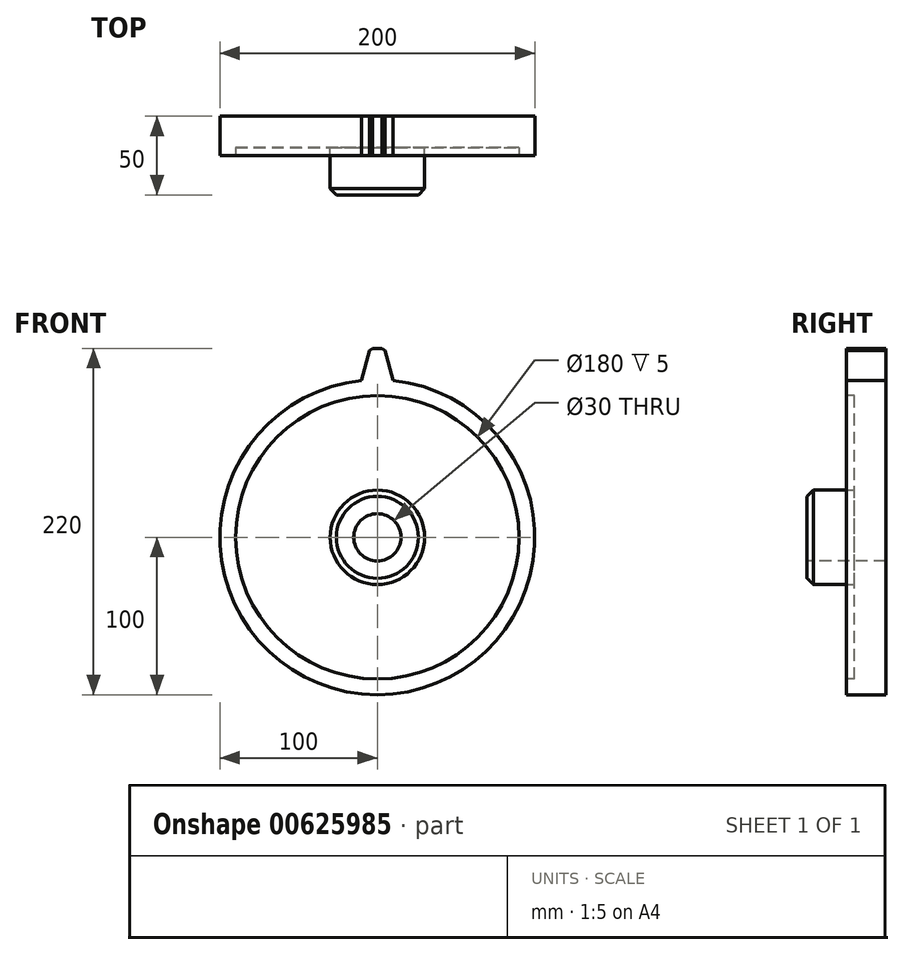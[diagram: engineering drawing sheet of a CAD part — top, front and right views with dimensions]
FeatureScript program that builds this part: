
annotation { "Feature Type Name" : "Feature", "Feature Type Description" : "" }
export const myFeature = defineFeature(function(context is Context, id is Id, definition is map)
    precondition{}
    {
        {
            var Q0;
            Q0=qCreatedBy(makeId("Front.planeOp"),FACE);
            var sketch = newSketch(context, id + "F0", { "sketchPlane" : qUnion([Q0])});
            skCircle(sketch, "E0", {"center": v(0, 0) * mm, "radius": 100 * mm});
            skSolve(sketch);
        }
        {
            var Q0;
            Q0 = qSketchRegion(id + "F0", true);
            extrude(context, id + "F1", {"entities" : qUnion([Q0]), "depth" : 25 * mm, "offsetDistance" : 25 * mm});
        }
        {
            var Q0;
            Q0=makeQuery(id+"F1.opExtrude","CAP_FACE",FACE,{"disambiguationData":[OSD([sQuery(id+"F0.wireOp",EDGE,"E0")])],"isStart":false});
            var sketch = newSketch(context, id + "F2", { "sketchPlane" : qUnion([Q0])});
            skLineSegment(sketch, "E1", {"start": v(-10, 99.5) * mm, "end": v(-4.5, 120) * mm});
            skLineSegment(sketch, "E2", {"start": v(-4.5, 120) * mm, "end": v(4.5, 120) * mm});
            skLineSegment(sketch, "E3", {"start": v(4.5, 120) * mm, "end": v(10, 99.5) * mm});
            skLineSegment(sketch, "E4", {"start": v(10, 99.5) * mm, "end": v(-10, 99.5) * mm});
            skSolve(sketch);
        }
        {
            var Q0;
            Q0 = qSketchRegion(id + "F2", true);
            extrude(context, id + "F3", {"entities" : qUnion([Q0]), "operationType" : NewBodyOperationType.ADD, "oppositeDirection" : true, "depth" : 25 * mm, "offsetDistance" : 25 * mm});
        }
        {
            var Q0;
            Q0=makeQuery(id+"F3.opExtrude","SWEPT_EDGE",EDGE,{"disambiguationData":[OSD([sQuery(id+"F0.wireOp",EDGE,"E0"),sQuery(id+"F2.wireOp",EDGE,"E3"),sQuery(id+"F2.wireOp",EDGE,"E4")])]});
            var Q1;
            Q1=makeQuery(id+"F3.opExtrude","SWEPT_EDGE",EDGE,{"disambiguationData":[OSD([sQuery(id+"F0.wireOp",EDGE,"E0"),sQuery(id+"F2.wireOp",EDGE,"E1"),sQuery(id+"F2.wireOp",EDGE,"E4")])]});
            fillet(context, id + "F4", {"entities" : qUnion([Q0, Q1]), "radius" : 5 * mm, "tangentPropagation" : true, "allowEdgeOverflow" : false});
        }
        {
            var Q0;
            Q0=makeQuery(id+"F3.opExtrude","SWEPT_EDGE",EDGE,{"disambiguationData":[OSD([sQuery(id+"F2.wireOp",EDGE,"E1"),sQuery(id+"F2.wireOp",EDGE,"E2")])]});
            var Q1;
            Q1=makeQuery(id+"F3.opExtrude","SWEPT_EDGE",EDGE,{"disambiguationData":[OSD([sQuery(id+"F2.wireOp",EDGE,"E2"),sQuery(id+"F2.wireOp",EDGE,"E3")])]});
            chamfer(context, id + "F5", {"entities" : qUnion([Q0, Q1]), "width" : 2 * mm, "tangentPropagation" : true});
        }
        {
            var Q0;
            {var subQ0=sQuery(id+"F2.wireOp",EDGE,"E4");var subQ1=sQuery(id+"F2.wireOp",EDGE,"E3");var subQ2=sQuery(id+"F2.wireOp",EDGE,"E2");var subQ3=sQuery(id+"F2.wireOp",EDGE,"E1");Q0=makeQuery(id+"FDIh3SWYxGmvvfI_1.19.F3.boolean.opBoolean","MERGE",FACE,{"derivedFrom":[makeQuery(id+"FDIh3SWYxGmvvfI_1.18.F3.boolean.opBoolean","MERGE",FACE,{"derivedFrom":[makeQuery(id+"FDIh3SWYxGmvvfI_1.17.F3.boolean.opBoolean","MERGE",FACE,{"derivedFrom":[makeQuery(id+"FDIh3SWYxGmvvfI_1.16.F3.boolean.opBoolean","MERGE",FACE,{"derivedFrom":[makeQuery(id+"FDIh3SWYxGmvvfI_1.15.F3.boolean.opBoolean","MERGE",FACE,{"derivedFrom":[makeQuery(id+"FDIh3SWYxGmvvfI_1.14.F3.boolean.opBoolean","MERGE",FACE,{"derivedFrom":[makeQuery(id+"FDIh3SWYxGmvvfI_1.13.F3.boolean.opBoolean","MERGE",FACE,{"derivedFrom":[makeQuery(id+"FDIh3SWYxGmvvfI_1.12.F3.boolean.opBoolean","MERGE",FACE,{"derivedFrom":[makeQuery(id+"FDIh3SWYxGmvvfI_1.11.F3.boolean.opBoolean","MERGE",FACE,{"derivedFrom":[makeQuery(id+"FDIh3SWYxGmvvfI_1.10.F3.boolean.opBoolean","MERGE",FACE,{"derivedFrom":[makeQuery(id+"FDIh3SWYxGmvvfI_1.9.F3.boolean.opBoolean","MERGE",FACE,{"derivedFrom":[makeQuery(id+"FDIh3SWYxGmvvfI_1.8.F3.boolean.opBoolean","MERGE",FACE,{"derivedFrom":[makeQuery(id+"FDIh3SWYxGmvvfI_1.7.F3.boolean.opBoolean","MERGE",FACE,{"derivedFrom":[makeQuery(id+"FDIh3SWYxGmvvfI_1.6.F3.boolean.opBoolean","MERGE",FACE,{"derivedFrom":[makeQuery(id+"FDIh3SWYxGmvvfI_1.5.F3.boolean.opBoolean","MERGE",FACE,{"derivedFrom":[makeQuery(id+"FDIh3SWYxGmvvfI_1.4.F3.boolean.opBoolean","MERGE",FACE,{"derivedFrom":[makeQuery(id+"FDIh3SWYxGmvvfI_1.3.F3.boolean.opBoolean","MERGE",FACE,{"derivedFrom":[makeQuery(id+"FDIh3SWYxGmvvfI_1.2.F3.boolean.opBoolean","MERGE",FACE,{"derivedFrom":[makeQuery(id+"FDIh3SWYxGmvvfI_1.1.F3.boolean.opBoolean","MERGE",FACE,{"derivedFrom":[makeQuery(id+"F3.boolean.opBoolean","MERGE",FACE,{"derivedFrom":[makeQuery(id+"F1.opExtrude","CAP_FACE",FACE,{"disambiguationData":[OSD([sQuery(id+"F0.wireOp",EDGE,"E0")])],"isStart":false}),makeQuery(id+"F3.opExtrude","CAP_FACE",FACE,{"disambiguationData":[OSD([subQ3,subQ2,subQ1,subQ0])],"isStart":true})]}),makeQuery(id+"FDIh3SWYxGmvvfI_1.1.F3.opExtrude","CAP_FACE",FACE,{"disambiguationData":[OSD([subQ3,subQ2,subQ1,subQ0])],"isStart":true})]}),makeQuery(id+"FDIh3SWYxGmvvfI_1.2.F3.opExtrude","CAP_FACE",FACE,{"disambiguationData":[OSD([subQ3,subQ2,subQ1,subQ0])],"isStart":true})]}),makeQuery(id+"FDIh3SWYxGmvvfI_1.3.F3.opExtrude","CAP_FACE",FACE,{"disambiguationData":[OSD([subQ3,subQ2,subQ1,subQ0])],"isStart":true})]}),makeQuery(id+"FDIh3SWYxGmvvfI_1.4.F3.opExtrude","CAP_FACE",FACE,{"disambiguationData":[OSD([subQ3,subQ2,subQ1,subQ0])],"isStart":true})]}),makeQuery(id+"FDIh3SWYxGmvvfI_1.5.F3.opExtrude","CAP_FACE",FACE,{"disambiguationData":[OSD([subQ3,subQ2,subQ1,subQ0])],"isStart":true})]}),makeQuery(id+"FDIh3SWYxGmvvfI_1.6.F3.opExtrude","CAP_FACE",FACE,{"disambiguationData":[OSD([subQ3,subQ2,subQ1,subQ0])],"isStart":true})]}),makeQuery(id+"FDIh3SWYxGmvvfI_1.7.F3.opExtrude","CAP_FACE",FACE,{"disambiguationData":[OSD([subQ3,subQ2,subQ1,subQ0])],"isStart":true})]}),makeQuery(id+"FDIh3SWYxGmvvfI_1.8.F3.opExtrude","CAP_FACE",FACE,{"disambiguationData":[OSD([subQ3,subQ2,subQ1,subQ0])],"isStart":true})]}),makeQuery(id+"FDIh3SWYxGmvvfI_1.9.F3.opExtrude","CAP_FACE",FACE,{"disambiguationData":[OSD([subQ3,subQ2,subQ1,subQ0])],"isStart":true})]}),makeQuery(id+"FDIh3SWYxGmvvfI_1.10.F3.opExtrude","CAP_FACE",FACE,{"disambiguationData":[OSD([subQ3,subQ2,subQ1,subQ0])],"isStart":true})]}),makeQuery(id+"FDIh3SWYxGmvvfI_1.11.F3.opExtrude","CAP_FACE",FACE,{"disambiguationData":[OSD([subQ3,subQ2,subQ1,subQ0])],"isStart":true})]}),makeQuery(id+"FDIh3SWYxGmvvfI_1.12.F3.opExtrude","CAP_FACE",FACE,{"disambiguationData":[OSD([subQ3,subQ2,subQ1,subQ0])],"isStart":true})]}),makeQuery(id+"FDIh3SWYxGmvvfI_1.13.F3.opExtrude","CAP_FACE",FACE,{"disambiguationData":[OSD([subQ3,subQ2,subQ1,subQ0])],"isStart":true})]}),makeQuery(id+"FDIh3SWYxGmvvfI_1.14.F3.opExtrude","CAP_FACE",FACE,{"disambiguationData":[OSD([subQ3,subQ2,subQ1,subQ0])],"isStart":true})]}),makeQuery(id+"FDIh3SWYxGmvvfI_1.15.F3.opExtrude","CAP_FACE",FACE,{"disambiguationData":[OSD([subQ3,subQ2,subQ1,subQ0])],"isStart":true})]}),makeQuery(id+"FDIh3SWYxGmvvfI_1.16.F3.opExtrude","CAP_FACE",FACE,{"disambiguationData":[OSD([subQ3,subQ2,subQ1,subQ0])],"isStart":true})]}),makeQuery(id+"FDIh3SWYxGmvvfI_1.17.F3.opExtrude","CAP_FACE",FACE,{"disambiguationData":[OSD([subQ3,subQ2,subQ1,subQ0])],"isStart":true})]}),makeQuery(id+"FDIh3SWYxGmvvfI_1.18.F3.opExtrude","CAP_FACE",FACE,{"disambiguationData":[OSD([subQ3,subQ2,subQ1,subQ0])],"isStart":true})]}),makeQuery(id+"FDIh3SWYxGmvvfI_1.19.F3.opExtrude","CAP_FACE",FACE,{"disambiguationData":[OSD([subQ3,subQ2,subQ1,subQ0])],"isStart":true})]});}
            var sketch = newSketch(context, id + "F6", { "sketchPlane" : qUnion([Q0])});
            skCircle(sketch, "E5", {"center": v(0, 0) * mm, "radius": 90 * mm});
            skSolve(sketch);
        }
        {
            var Q0;
            Q0=makeQuery(id+"F6.imprint","IMPRINT",FACE,{"disambiguationData":[TD([[makeQuery(id+"F6.imprint","IMPRINT",EDGE,{"derivedFrom":sQuery(id+"F6.wireOp",EDGE,"E5")}),1.0]])]});
            extrude(context, id + "F7", {"entities" : qUnion([Q0]), "operationType" : NewBodyOperationType.REMOVE, "oppositeDirection" : true, "depth" : 5 * mm, "offsetDistance" : 25 * mm});
        }
        {
            var Q0;
            Q0=makeQuery(id+"F7.boolean.opBoolean","COPY",FACE,{"derivedFrom":makeQuery(id+"F7.opExtrude","CAP_FACE",FACE,{"disambiguationData":[OSD([sQuery(id+"F6.wireOp",EDGE,"E5")])],"isStart":false})});
            var sketch = newSketch(context, id + "F8", { "sketchPlane" : qUnion([Q0])});
            skCircle(sketch, "E6", {"center": v(0, 0) * mm, "radius": 30 * mm});
            skSolve(sketch);
        }
        {
            var Q0;
            Q0=makeQuery(id+"F8.imprint","IMPRINT",FACE,{"disambiguationData":[TD([[makeQuery(id+"F8.imprint","IMPRINT",EDGE,{"derivedFrom":sQuery(id+"F8.wireOp",EDGE,"E6")}),1.0]])]});
            extrude(context, id + "F9", {"entities" : qUnion([Q0]), "operationType" : NewBodyOperationType.ADD, "depth" : 30 * mm, "offsetDistance" : 25 * mm});
        }
        {
            var Q0;
            Q0=makeQuery(id+"F9.opExtrude","CAP_FACE",FACE,{"disambiguationData":[OSD([sQuery(id+"F8.wireOp",EDGE,"E6")])],"isStart":false});
            var sketch = newSketch(context, id + "F10", { "sketchPlane" : qUnion([Q0])});
            skCircle(sketch, "E7", {"center": v(0, 0) * mm, "radius": 15 * mm});
            skSolve(sketch);
        }
        {
            var Q0;
            Q0 = qSketchRegion(id + "F10", true);
            extrude(context, id + "F11", {"entities" : qUnion([Q0]), "operationType" : NewBodyOperationType.REMOVE, "endBound" : BoundingType.THROUGH_ALL, "oppositeDirection" : true, "depth" : 25 * mm, "offsetDistance" : 25 * mm});
        }
        {
            var Q0;
            Q0=makeQuery(id+"F9.opExtrude","CAP_EDGE",EDGE,{"disambiguationData":[OSD([sQuery(id+"F8.wireOp",EDGE,"E6")])],"isStart":false});
            var Q1;
            Q1=makeQuery(id+"F11.boolean.opBoolean","COPY",EDGE,{"derivedFrom":makeQuery(id+"F11.opExtrude","CAP_EDGE",EDGE,{"disambiguationData":[OSD([sQuery(id+"F10.wireOp",EDGE,"E7")])],"isStart":true})});
            chamfer(context, id + "F12", {"entities" : qUnion([Q0, Q1]), "width" : 4 * mm, "tangentPropagation" : true});
        }
    });
